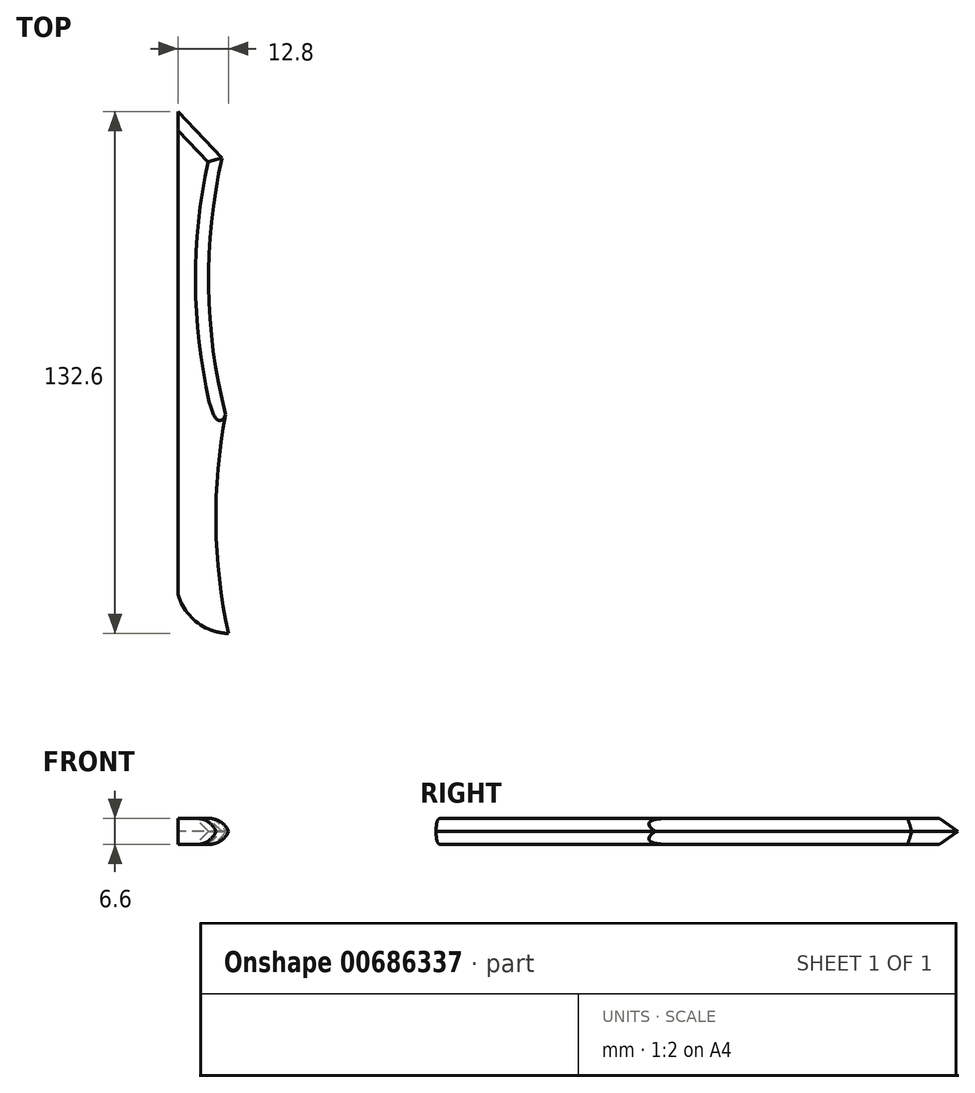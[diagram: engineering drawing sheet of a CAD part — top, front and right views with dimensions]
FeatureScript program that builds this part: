
annotation { "Feature Type Name" : "Feature", "Feature Type Description" : "" }
export const myFeature = defineFeature(function(context is Context, id is Id, definition is map)
    precondition{}
    {
        {
            var Q0;
            Q0=qCreatedBy(makeId("Top.planeOp"),FACE);
            var sketch = newSketch(context, id + "F0", { "sketchPlane" : qUnion([Q0])});
            skLineSegment(sketch, "E0.left", {"start": v(0, 0) * mm, "end": v(0, 76.28) * mm});
            skPoint(sketch, "E1.oppositeSnap0", {"position": v(13.13, 0) * mm});
            skLineSegment(sketch, "E1.bottom", {"start": v(0, 0) * mm, "end": v(13.13, 0) * mm});
            skLineSegment(sketch, "E2", {"start": v(0, 76.28) * mm, "end": v(13.13, 62.44) * mm});
            skArc(sketch, "E3", {"start": v(13.13, 62.44) * mm, "mid": v(9.49, 31.22) * mm, "end": v(13.13, 0) * mm});
            skArc(sketch, "E4", {"start": v(13.13, 0) * mm, "mid": v(9.9, -29.45) * mm, "end": v(13.13, -58.9) * mm});
            skArc(sketch, "E5", {"start": v(0, -48.97) * mm, "mid": v(4.9, -56.14) * mm, "end": v(13.13, -58.9) * mm});
            skLineSegment(sketch, "E6", {"start": v(0, 0) * mm, "end": v(0, -48.97) * mm});
            skSolve(sketch);
        }
        {
            var Q0;
            Q0 = qSketchRegion(id + "F0", true);
            extrude(context, id + "F1", {"entities" : qUnion([Q0]), "depth" : 6.6 * mm, "offsetDistance" : 25.4 * mm});
        }
        {
            var Q0;
            Q0=makeQuery(id+"F1.opExtrude","CAP_EDGE",EDGE,{"disambiguationData":[OSD([sQuery(id+"F0.wireOp",EDGE,"E3")])],"isStart":false});
            var Q1;
            Q1=makeQuery(id+"F1.opExtrude","CAP_EDGE",EDGE,{"disambiguationData":[OSD([sQuery(id+"F0.wireOp",EDGE,"E3")])],"isStart":true});
            chamfer(context, id + "F2", {"entities" : qUnion([Q0, Q1]), "width" : 5.08 * mm, "tangentPropagation" : true});
        }
        {
            var Q0;
            Q0=makeQuery(id+"F1.opExtrude","CAP_EDGE",EDGE,{"disambiguationData":[OSD([sQuery(id+"F0.wireOp",EDGE,"E2")])],"isStart":true});
            var Q1;
            Q1=makeQuery(id+"F1.opExtrude","CAP_EDGE",EDGE,{"disambiguationData":[OSD([sQuery(id+"F0.wireOp",EDGE,"E2")])],"isStart":false});
            chamfer(context, id + "F3", {"entities" : qUnion([Q0, Q1]), "width" : 5.08 * mm, "tangentPropagation" : true});
        }
        {
            var Q0;
            Q0=makeQuery(id+"F1.opExtrude","CAP_EDGE",EDGE,{"disambiguationData":[OSD([sQuery(id+"F0.wireOp",EDGE,"E4")])],"isStart":false});
            var Q1;
            Q1=makeQuery(id+"F1.opExtrude","CAP_EDGE",EDGE,{"disambiguationData":[OSD([sQuery(id+"F0.wireOp",EDGE,"E4")])],"isStart":true});
            fillet(context, id + "F4", {"entities" : qUnion([Q0, Q1]), "radius" : 5.08 * mm, "tangentPropagation" : true, "allowEdgeOverflow" : false});
        }
    });
